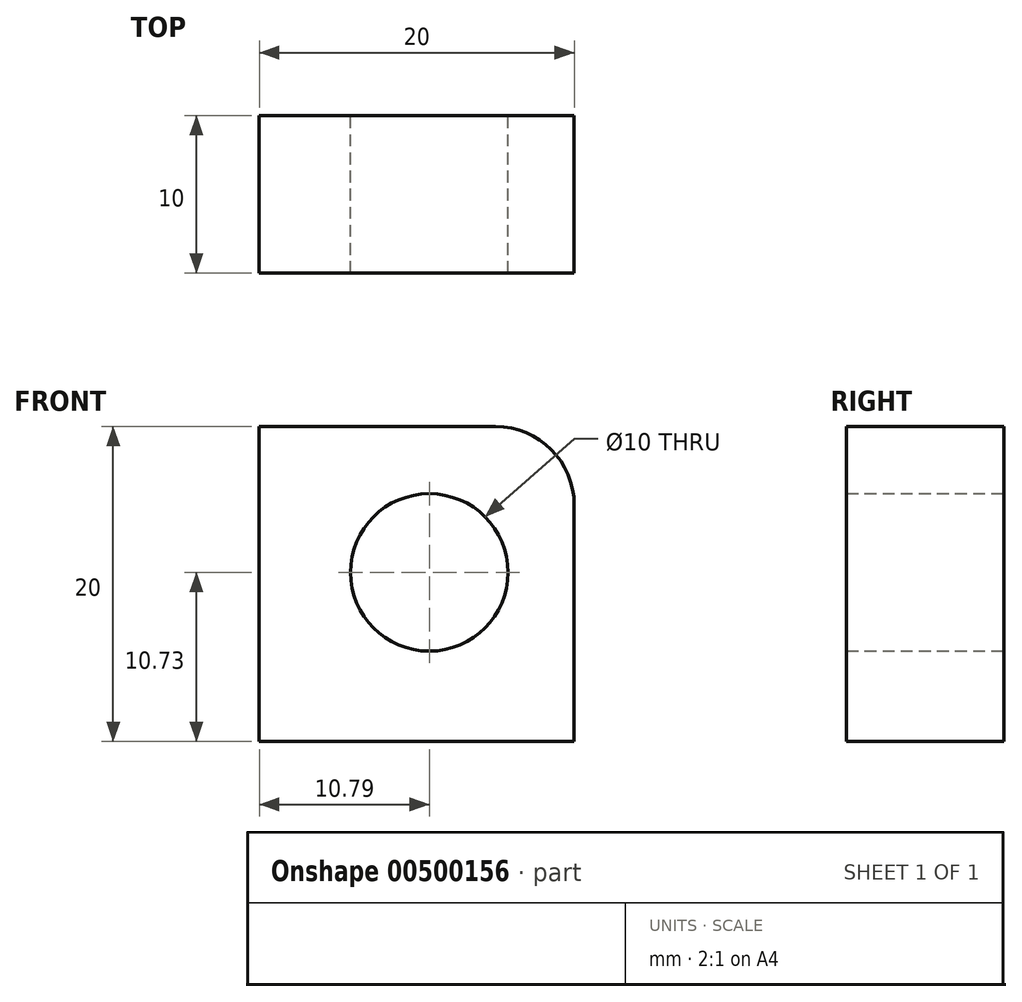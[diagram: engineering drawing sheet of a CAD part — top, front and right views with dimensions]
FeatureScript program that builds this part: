
annotation { "Feature Type Name" : "Feature", "Feature Type Description" : "" }
export const myFeature = defineFeature(function(context is Context, id is Id, definition is map)
    precondition{}
    {
        {
            var Q0;
            Q0=qCreatedBy(makeId("Front.planeOp"),FACE);
            var sketch = newSketch(context, id + "F0", { "sketchPlane" : qUnion([Q0])});
            skCircle(sketch, "E0", {"center": v(0, 0) * mm, "radius": 5 * mm});
            skLineSegment(sketch, "E1.bottom", {"start": v(-10.8, 9.27) * mm, "end": v(4.2, 9.27) * mm});
            skLineSegment(sketch, "E1.top", {"start": v(-10.8, -10.73) * mm, "end": v(9.2, -10.73) * mm});
            skLineSegment(sketch, "E1.left", {"start": v(-10.8, 9.27) * mm, "end": v(-10.8, -10.73) * mm});
            skLineSegment(sketch, "E1.right", {"start": v(9.2, 4.27) * mm, "end": v(9.2, -10.73) * mm});
            skLineSegment(sketch, "E2.top", {"start": v(-0.8, 9.27) * mm, "end": v(0, 9.27) * mm});
            skPoint(sketch, "E3.visualSharp", {"position": v(9.2, 9.27) * mm});
            skArc(sketch, "E3.filletArc", {"start": v(9.2, 4.27) * mm, "mid": v(7.74, 7.8) * mm, "end": v(4.2, 9.27) * mm});
            skSolve(sketch);
        }
        {
            var Q0;
            Q0=makeQuery(id+"F0.imprint","IMPRINT",FACE,{"disambiguationData":[TD([[makeQuery(id+"F0.imprint","IMPRINT",EDGE,{"derivedFrom":sQuery(id+"F0.wireOp",EDGE,"E0")}),-1.0]])]});
            var Q1;
            Q1 = qSketchRegion(id + "F0", true);
            extrude(context, id + "F1", {"entities" : qUnion([Q0, Q1]), "depth" : 10 * mm});
        }
    });
